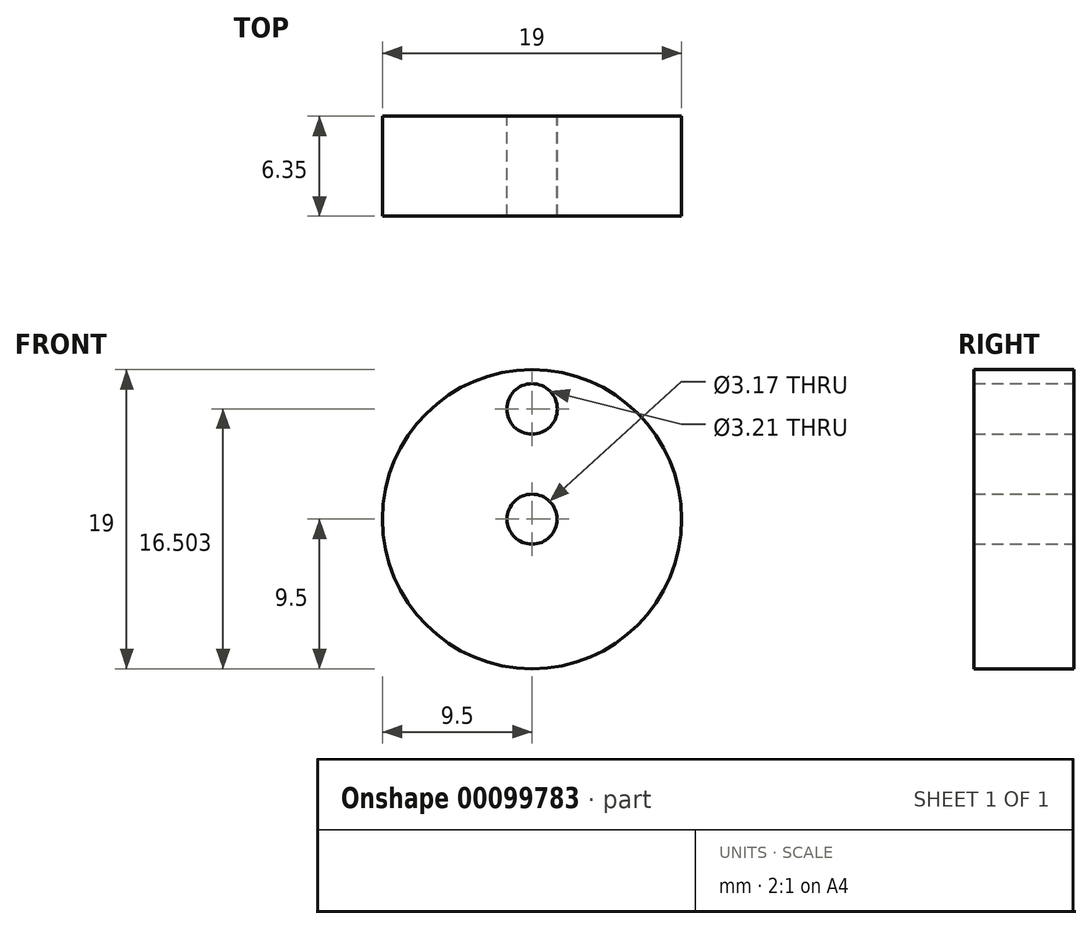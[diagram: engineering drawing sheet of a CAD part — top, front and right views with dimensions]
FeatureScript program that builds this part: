
annotation { "Feature Type Name" : "Feature", "Feature Type Description" : "" }
export const myFeature = defineFeature(function(context is Context, id is Id, definition is map)
    precondition{}
    {
        {
            var Q0;
            Q0=qCreatedBy(makeId("Front.planeOp"),FACE);
            var sketch = newSketch(context, id + "F0", { "sketchPlane" : qUnion([Q0])});
            skCircle(sketch, "E0", {"center": v(0, 0) * mm, "radius": 9.5 * mm});
            skCircle(sketch, "E1", {"center": v(0, 0) * mm, "radius": 1.59 * mm});
            skCircle(sketch, "E2", {"center": v(0, 7) * mm, "radius": 1.6 * mm});
            skSolve(sketch);
        }
        {
            var Q0;
            Q0=makeQuery(id+"F0.imprint","IMPRINT",FACE,{"disambiguationData":[TD([[makeQuery(id+"F0.imprint","IMPRINT",EDGE,{"derivedFrom":sQuery(id+"F0.wireOp",EDGE,"E0")}),1.0]])]});
            extrude(context, id + "F1", {"entities" : qUnion([Q0]), "depth" : 6.35 * mm});
        }
    });
